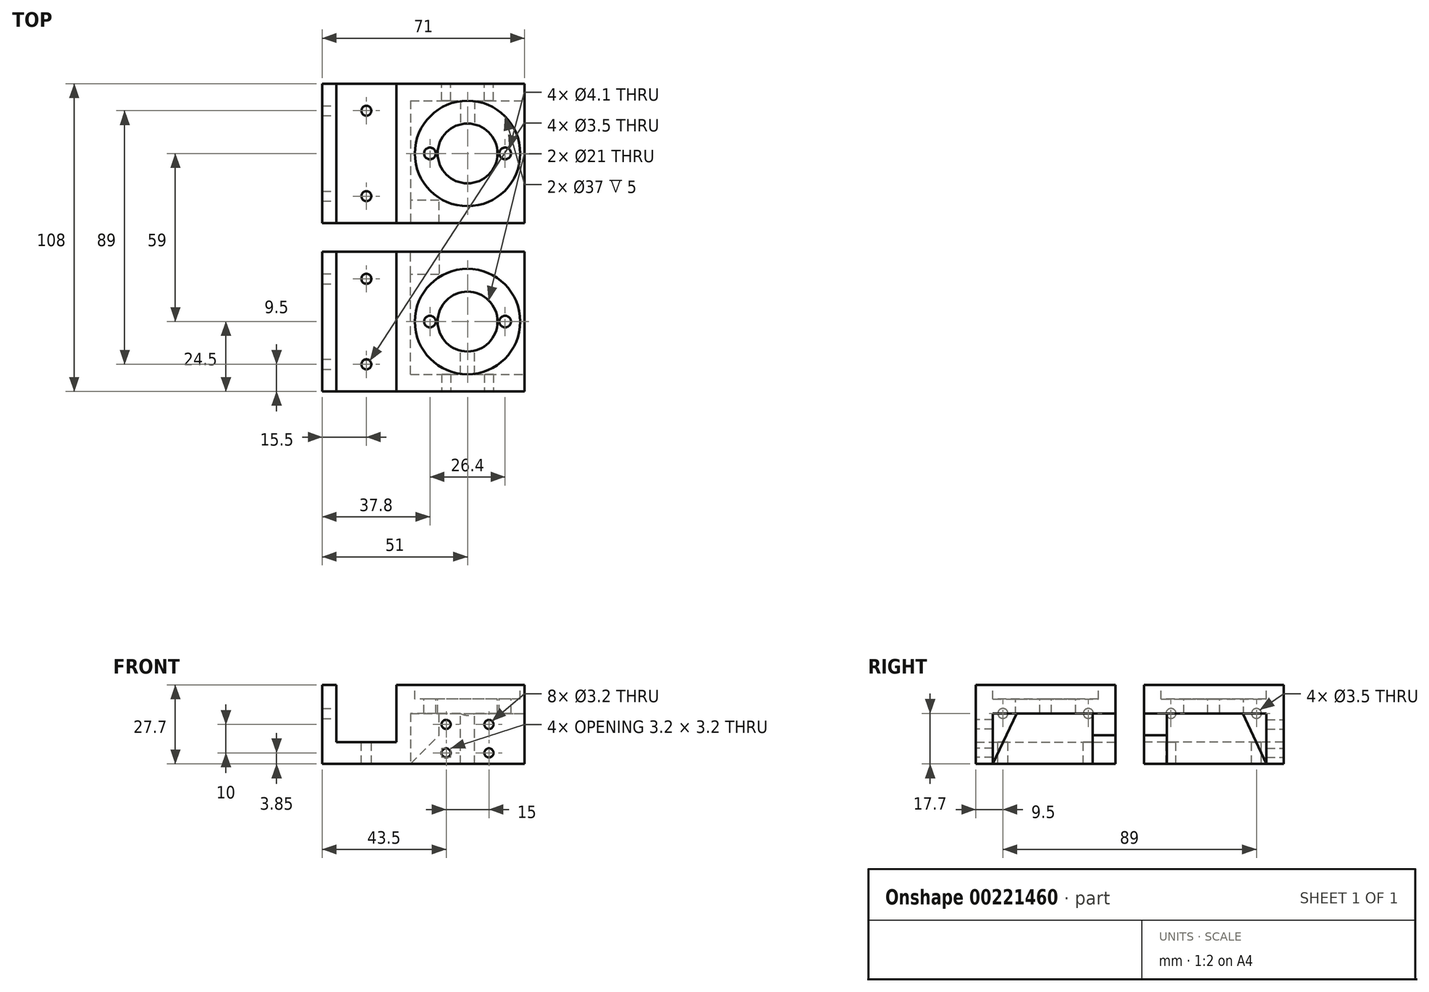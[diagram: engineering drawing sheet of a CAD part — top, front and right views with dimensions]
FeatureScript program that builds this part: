
annotation { "Feature Type Name" : "Feature", "Feature Type Description" : "" }
export const myFeature = defineFeature(function(context is Context, id is Id, definition is map)
    precondition{}
    {
        {
            var Q0;
            Q0=qCreatedBy(makeId("Front.planeOp"),FACE);
            var sketch = newSketch(context, id + "F0", { "sketchPlane" : qUnion([Q0])});
            skLineSegment(sketch, "E0.bottom", {"start": v(0, 0) * mm, "end": v(27, 0) * mm, "construction": true});
            skLineSegment(sketch, "E0.top", {"start": v(0, 27.7) * mm, "end": v(27, 27.7) * mm, "construction": true});
            skLineSegment(sketch, "E0.left", {"start": v(0, 0) * mm, "end": v(0, 27.7) * mm, "construction": true});
            skLineSegment(sketch, "E0.right", {"start": v(27, 0) * mm, "end": v(27, 27.7) * mm, "construction": true});
            skLineSegment(sketch, "E1.bottom", {"start": v(-6.5, 27.7) * mm, "end": v(33.5, 27.7) * mm});
            skLineSegment(sketch, "E1.top", {"start": v(-6.5, 0) * mm, "end": v(33.5, 0) * mm});
            skLineSegment(sketch, "E1.left", {"start": v(-6.5, 27.7) * mm, "end": v(-6.5, 0) * mm});
            skLineSegment(sketch, "E1.right", {"start": v(33.5, 27.7) * mm, "end": v(33.5, 0) * mm});
            skSolve(sketch);
        }
        {
            var Q0;
            Q0=makeQuery(id+"F0.imprint","IMPRINT",FACE,{"disambiguationData":[TD([[makeQuery(id+"F0.imprint","IMPRINT",EDGE,{"derivedFrom":sQuery(id+"F0.wireOp",EDGE,"E0.bottom")}),1.0]])]});
            var Q1;
            Q1=makeQuery(id+"F0.imprint","IMPRINT",FACE,{"disambiguationData":[TD([[makeQuery(id+"F0.imprint","IMPRINT",EDGE,{"derivedFrom":sQuery(id+"F0.wireOp",EDGE,"E1.bottom")}),-1.0]])]});
            extrude(context, id + "F1", {"entities" : qUnion([Q0, Q1]), "depth" : 6 * mm});
        }
        {
            var Q0;
            Q0=makeQuery(id+"F1.opExtrude","CAP_FACE",FACE,{"disambiguationData":[OSD([sQuery(id+"F0.wireOp",EDGE,"E1.bottom"),sQuery(id+"F0.wireOp",EDGE,"E1.top"),sQuery(id+"F0.wireOp",EDGE,"E1.left"),sQuery(id+"F0.wireOp",EDGE,"E1.right")])],"isStart":false});
            var sketch = newSketch(context, id + "F2", { "sketchPlane" : qUnion([Q0])});
            skLineSegment(sketch, "E2.bottom", {"start": v(-6.5, 27.7) * mm, "end": v(33.5, 27.7) * mm});
            skLineSegment(sketch, "E2.top", {"start": v(-6.5, 17.7) * mm, "end": v(33.5, 17.7) * mm});
            skLineSegment(sketch, "E2.left", {"start": v(-6.5, 27.7) * mm, "end": v(-6.5, 17.7) * mm});
            skLineSegment(sketch, "E2.right", {"start": v(33.5, 27.7) * mm, "end": v(33.5, 17.7) * mm});
            skLineSegment(sketch, "E3", {"start": v(13.5, 27.7) * mm, "end": v(13.5, 0) * mm, "construction": true});
            skSolve(sketch);
        }
        {
            var Q0;
            Q0=makeQuery(id+"F2.imprint","IMPRINT",FACE,{"disambiguationData":[TD([[makeQuery(id+"F2.imprint","IMPRINT",EDGE,{"derivedFrom":sQuery(id+"F2.wireOp",EDGE,"E2.bottom")}),-1.0]])]});
            extrude(context, id + "F3", {"entities" : qUnion([Q0]), "operationType" : NewBodyOperationType.ADD, "depth" : 43 * mm});
        }
        {
            var Q0;
            Q0=makeQuery(id+"F3.opExtrude","SWEPT_FACE",FACE,{"disambiguationData":[OSD([sQuery(id+"F2.wireOp",EDGE,"E2.bottom")])]});
            var sketch = newSketch(context, id + "F4", { "sketchPlane" : qUnion([Q0])});
            skCircle(sketch, "E4", {"center": v(13.5, -24.5) * mm, "radius": 18.5 * mm});
            skPoint(sketch, "E4.centerSnap0", {"position": v(13.5, -3) * mm});
            skPoint(sketch, "E4.centerSnap1", {"position": v(-6.5, -24.5) * mm});
            skSolve(sketch);
        }
        {
            var Q0;
            Q0=makeQuery(id+"F4.imprint","IMPRINT",FACE,{"disambiguationData":[TD([[makeQuery(id+"F4.imprint","IMPRINT",EDGE,{"derivedFrom":sQuery(id+"F4.wireOp",EDGE,"E4")}),1.0]])]});
            extrude(context, id + "F5", {"entities" : qUnion([Q0]), "operationType" : NewBodyOperationType.REMOVE, "oppositeDirection" : true, "depth" : 5 * mm});
        }
        {
            var Q0;
            Q0=makeQuery(id+"F5.boolean.opBoolean","COPY",FACE,{"derivedFrom":makeQuery(id+"F5.opExtrude","CAP_FACE",FACE,{"disambiguationData":[OSD([sQuery(id+"F4.wireOp",EDGE,"E4")])],"isStart":false})});
            var sketch = newSketch(context, id + "F6", { "sketchPlane" : qUnion([Q0])});
            skCircle(sketch, "E5", {"center": v(13.5, -24.5) * mm, "radius": 10.5 * mm});
            skLineSegment(sketch, "E6", {"start": v(13.5, -24.5) * mm, "end": v(32, -24.5) * mm, "construction": true});
            skLineSegment(sketch, "E7", {"start": v(13.5, -24.5) * mm, "end": v(-5, -24.5) * mm, "construction": true});
            skCircle(sketch, "E8", {"center": v(13.5, -24.5) * mm, "radius": 13.2 * mm, "construction": true});
            skCircle(sketch, "E9", {"center": v(26.7, -24.5) * mm, "radius": 2.05 * mm});
            skCircle(sketch, "E10", {"center": v(0.3, -24.5) * mm, "radius": 2.05 * mm});
            skSolve(sketch);
        }
        {
            var Q0;
            Q0 = qSketchRegion(id + "F6", true);
            extrude(context, id + "F7", {"entities" : qUnion([Q0]), "operationType" : NewBodyOperationType.REMOVE, "endBound" : BoundingType.THROUGH_ALL, "oppositeDirection" : true, "depth" : 25 * mm});
        }
        {
            var Q0;
            Q0=makeQuery(id+"F3.boolean.opBoolean","MERGE",FACE,{"derivedFrom":[makeQuery(id+"F1.opExtrude","SWEPT_FACE",FACE,{"disambiguationData":[OSD([sQuery(id+"F0.wireOp",EDGE,"E1.left")])]}),makeQuery(id+"F3.opExtrude","SWEPT_FACE",FACE,{"disambiguationData":[OSD([sQuery(id+"F2.wireOp",EDGE,"E2.left")])]})]});
            var sketch = newSketch(context, id + "F8", { "sketchPlane" : qUnion([Q0])});
            skLineSegment(sketch, "E11.bottom", {"start": v(0, 0) * mm, "end": v(49, 0) * mm});
            skLineSegment(sketch, "E11.top", {"start": v(0, 27.7) * mm, "end": v(49, 27.7) * mm});
            skLineSegment(sketch, "E11.left", {"start": v(0, 0) * mm, "end": v(0, 27.7) * mm});
            skLineSegment(sketch, "E11.right", {"start": v(49, 0) * mm, "end": v(49, 27.7) * mm});
            skSolve(sketch);
        }
        {
            var Q0;
            {var subQ1=sQuery(id+"F2.wireOp",EDGE,"E2.top");var subQ2=sQuery(id+"F2.wireOp",EDGE,"E2.left");var subQ3=sQuery(id+"F0.wireOp",EDGE,"E1.left");var subQ8=makeQuery(id+"F3.opExtrude","SWEPT_EDGE",EDGE,{"disambiguationData":[OSD([subQ3,subQ1,subQ2])]});Q0=makeQuery(id+"F8.imprint","IMPRINT",FACE,{"disambiguationData":[TD([[makeQuery(id+"F8.imprint","IMPRINT",EDGE,{"derivedFrom":subQ8}),1.0]])]});}
            var Q1;
            {var subQ12=sQuery(id+"F8.wireOp",EDGE,"E11.left");Q1=makeQuery(id+"F8.imprint","IMPRINT",FACE,{"disambiguationData":[TD([[makeQuery(id+"F8.imprint","IMPRINT",EDGE,{"derivedFrom":subQ12}),1.0]])]});}
            extrude(context, id + "F9", {"entities" : qUnion([Q0, Q1]), "operationType" : NewBodyOperationType.ADD, "depth" : 31 * mm});
        }
        {
            var Q0;
            Q0=makeQuery(id+"F9.boolean.opBoolean","MERGE",FACE,{"derivedFrom":[makeQuery(id+"F3.opExtrude","CAP_FACE",FACE,{"disambiguationData":[OSD([sQuery(id+"F2.wireOp",EDGE,"E2.bottom"),sQuery(id+"F2.wireOp",EDGE,"E2.top"),sQuery(id+"F2.wireOp",EDGE,"E2.left"),sQuery(id+"F2.wireOp",EDGE,"E2.right")])],"isStart":false}),makeQuery(id+"F9.opExtrude","SWEPT_FACE",FACE,{"disambiguationData":[OSD([sQuery(id+"F8.wireOp",EDGE,"E11.right")])]})]});
            var sketch = newSketch(context, id + "F10", { "sketchPlane" : qUnion([Q0])});
            skLineSegment(sketch, "E12", {"start": v(-32.5, 27.7) * mm, "end": v(-32.5, 7.7) * mm});
            skLineSegment(sketch, "E13", {"start": v(-32.5, 7.7) * mm, "end": v(-11.5, 7.7) * mm});
            skLineSegment(sketch, "E14", {"start": v(-11.5, 7.7) * mm, "end": v(-11.5, 27.7) * mm});
            skLineSegment(sketch, "E15", {"start": v(-32.5, 27.7) * mm, "end": v(-11.5, 27.7) * mm});
            skSolve(sketch);
        }
        {
            var Q0;
            Q0=makeQuery(id+"F10.imprint","IMPRINT",FACE,{"disambiguationData":[TD([[makeQuery(id+"F10.imprint","IMPRINT",EDGE,{"derivedFrom":sQuery(id+"F10.wireOp",EDGE,"E12")}),1.0]])]});
            extrude(context, id + "F11", {"entities" : qUnion([Q0]), "operationType" : NewBodyOperationType.REMOVE, "endBound" : BoundingType.THROUGH_ALL, "oppositeDirection" : true, "depth" : 25 * mm});
        }
        {
            var Q0;
            Q0=makeQuery(id+"F3.opExtrude","SWEPT_FACE",FACE,{"disambiguationData":[OSD([sQuery(id+"F2.wireOp",EDGE,"E2.top")])]});
            var sketch = newSketch(context, id + "F12", { "sketchPlane" : qUnion([Q0])});
            skLineSegment(sketch, "E16.bottom", {"start": v(11, 6) * mm, "end": v(16, 6) * mm});
            skLineSegment(sketch, "E16.left", {"start": v(11, 6) * mm, "end": v(11, 14.3) * mm});
            skLineSegment(sketch, "E16.right", {"start": v(16, 6) * mm, "end": v(16, 14.3) * mm});
            skArc(sketch, "E17", {"start": v(16, 14.3) * mm, "mid": v(13.5, 14) * mm, "end": v(11, 14.3) * mm});
            skPoint(sketch, "E18", {"position": v(13.5, 6) * mm});
            skSolve(sketch);
        }
        {
            var Q0;
            Q0=makeQuery(id+"F12.imprint","IMPRINT",FACE,{"disambiguationData":[TD([[makeQuery(id+"F12.imprint","IMPRINT",EDGE,{"derivedFrom":sQuery(id+"F12.wireOp",EDGE,"E16.bottom")}),1.0]])]});
            var Q1;
            Q1=makeQuery(id+"F9.boolean.opBoolean","MERGE",FACE,{"derivedFrom":[makeQuery(id+"F1.opExtrude","SWEPT_FACE",FACE,{"disambiguationData":[OSD([sQuery(id+"F0.wireOp",EDGE,"E1.top")])]}),makeQuery(id+"F9.opExtrude","SWEPT_FACE",FACE,{"disambiguationData":[OSD([sQuery(id+"F8.wireOp",EDGE,"E11.bottom")])]})]});
            extrude(context, id + "F13", {"entities" : qUnion([Q0]), "operationType" : NewBodyOperationType.ADD, "endBound" : BoundingType.UP_TO_SURFACE, "endBoundEntityFace" : qUnion([Q1]), "depth" : 25 * mm});
        }
        {
            var Q0;
            Q0=makeQuery(id+"F13.opExtrude","SWEPT_FACE",FACE,{"disambiguationData":[OSD([sQuery(id+"F12.wireOp",EDGE,"E16.right")])]});
            var sketch = newSketch(context, id + "F14", { "sketchPlane" : qUnion([Q0])});
            skLineSegment(sketch, "E19", {"start": v(-14.3, 17.7) * mm, "end": v(-6, 0) * mm});
            skLineSegment(sketch, "E20", {"start": v(-6, 0) * mm, "end": v(-6, 17.7) * mm});
            skLineSegment(sketch, "E21", {"start": v(-6, 17.7) * mm, "end": v(-14.3, 17.7) * mm});
            skSolve(sketch);
        }
        {
            var Q0;
            Q0=makeQuery(id+"F14.imprint","IMPRINT",FACE,{"disambiguationData":[TD([[makeQuery(id+"F14.imprint","IMPRINT",EDGE,{"derivedFrom":sQuery(id+"F14.wireOp",EDGE,"E19")}),-1.0]])]});
            var Q1;
            Q1=makeQuery(id+"F13.opExtrude","SWEPT_FACE",FACE,{"disambiguationData":[OSD([sQuery(id+"F12.wireOp",EDGE,"E16.left")])]});
            extrude(context, id + "F15", {"entities" : qUnion([Q0]), "operationType" : NewBodyOperationType.REMOVE, "endBound" : BoundingType.UP_TO_SURFACE, "oppositeDirection" : true, "endBoundEntityFace" : qUnion([Q1]), "depth" : 25 * mm});
        }
        {
            var Q0;
            Q0=makeQuery(id+"F9.opExtrude","CAP_FACE",FACE,{"disambiguationData":[OSD([sQuery(id+"F8.wireOp",EDGE,"E11.bottom"),sQuery(id+"F8.wireOp",EDGE,"E11.top"),sQuery(id+"F8.wireOp",EDGE,"E11.left"),sQuery(id+"F8.wireOp",EDGE,"E11.right")])],"isStart":true});
            var sketch = newSketch(context, id + "F16", { "sketchPlane" : qUnion([Q0])});
            skLineSegment(sketch, "E22.bottom", {"start": v(-49, 17.7) * mm, "end": v(-41, 17.7) * mm});
            skLineSegment(sketch, "E22.top", {"start": v(-49, 0) * mm, "end": v(-41, 0) * mm});
            skLineSegment(sketch, "E22.left", {"start": v(-49, 17.7) * mm, "end": v(-49, 0) * mm});
            skLineSegment(sketch, "E22.right", {"start": v(-41, 17.7) * mm, "end": v(-41, 0) * mm});
            skSolve(sketch);
        }
        {
            var Q0;
            Q0=makeQuery(id+"F16.imprint","IMPRINT",FACE,{"disambiguationData":[TD([[makeQuery(id+"F16.imprint","IMPRINT",EDGE,{"derivedFrom":sQuery(id+"F16.wireOp",EDGE,"E22.bottom")}),-1.0]])]});
            var Q1;
            Q1=makeQuery(id+"F16.imprint","IMPRINT",FACE,{"disambiguationData":[TD([[makeQuery(id+"F16.imprint","IMPRINT",EDGE,{"derivedFrom":sQuery(id+"F16.wireOp",EDGE,"8BEWw2aY-geet-BJQ8-Mbal-S3a0Wca1nJoR.bottom")}),-1.0]])]});
            extrude(context, id + "F17", {"entities" : qUnion([Q0, Q1]), "operationType" : NewBodyOperationType.ADD, "depth" : 10 * mm});
        }
        {
            var Q0;
            Q0=makeQuery(id+"F11.boolean.opBoolean","COPY",FACE,{"derivedFrom":makeQuery(id+"F11.opExtrude","SWEPT_FACE",FACE,{"disambiguationData":[OSD([sQuery(id+"F10.wireOp",EDGE,"E13")])]})});
            var sketch = newSketch(context, id + "F18", { "sketchPlane" : qUnion([Q0])});
            skLineSegment(sketch, "E23", {"start": v(-22, 0) * mm, "end": v(-22, -49) * mm, "construction": true});
            skCircle(sketch, "E24", {"center": v(-22, -9.5) * mm, "radius": 1.75 * mm});
            skCircle(sketch, "E25", {"center": v(-22, -39.5) * mm, "radius": 1.75 * mm});
            skSolve(sketch);
        }
        {
            var Q0;
            Q0=makeQuery(id+"F18.imprint","IMPRINT",FACE,{"disambiguationData":[TD([[makeQuery(id+"F18.imprint","IMPRINT",EDGE,{"derivedFrom":sQuery(id+"F18.wireOp",EDGE,"E25")}),1.0]])]});
            var Q1;
            Q1=makeQuery(id+"F18.imprint","IMPRINT",FACE,{"disambiguationData":[TD([[makeQuery(id+"F18.imprint","IMPRINT",EDGE,{"derivedFrom":sQuery(id+"F18.wireOp",EDGE,"E24")}),1.0]])]});
            extrude(context, id + "F19", {"entities" : qUnion([Q0, Q1]), "operationType" : NewBodyOperationType.REMOVE, "endBound" : BoundingType.THROUGH_ALL, "oppositeDirection" : true, "depth" : 25 * mm});
        }
        {
            var Q0;
            Q0=makeQuery(id+"F11.boolean.opBoolean","COPY",FACE,{"derivedFrom":makeQuery(id+"F11.opExtrude","SWEPT_FACE",FACE,{"disambiguationData":[OSD([sQuery(id+"F10.wireOp",EDGE,"E12")])]})});
            var sketch = newSketch(context, id + "F20", { "sketchPlane" : qUnion([Q0])});
            skLineSegment(sketch, "E26", {"start": v(-49, 17.7) * mm, "end": v(0, 17.7) * mm, "construction": true});
            skCircle(sketch, "E27", {"center": v(-39.5, 17.7) * mm, "radius": 1.75 * mm});
            skCircle(sketch, "E28", {"center": v(-9.5, 17.7) * mm, "radius": 1.75 * mm});
            skSolve(sketch);
        }
        {
            var Q0;
            Q0=makeQuery(id+"F20.imprint","IMPRINT",FACE,{"disambiguationData":[TD([[makeQuery(id+"F20.imprint","IMPRINT",EDGE,{"derivedFrom":sQuery(id+"F20.wireOp",EDGE,"E27")}),1.0]])]});
            var Q1;
            Q1=makeQuery(id+"F20.imprint","IMPRINT",FACE,{"disambiguationData":[TD([[makeQuery(id+"F20.imprint","IMPRINT",EDGE,{"derivedFrom":sQuery(id+"F20.wireOp",EDGE,"E28")}),1.0]])]});
            extrude(context, id + "F21", {"entities" : qUnion([Q0, Q1]), "operationType" : NewBodyOperationType.REMOVE, "endBound" : BoundingType.THROUGH_ALL, "oppositeDirection" : true, "depth" : 25 * mm});
        }
        {
            var Q0;
            {var subQ2=sQuery(id+"F0.wireOp",EDGE,"E1.top");var subQ3=makeQuery(id+"F1.opExtrude","SWEPT_FACE",FACE,{"disambiguationData":[OSD([subQ2])]});var subQ4=sQuery(id+"F0.wireOp",EDGE,"E1.right");var subQ5=sQuery(id+"F0.wireOp",EDGE,"E1.left");Q0=makeQuery(id+"F13.boolean.opBoolean","SPLIT",FACE,{"disambiguationData":[TD([makeQuery(id+"F13.opExtrude","SWEPT_FACE",FACE,{"disambiguationData":[OSD([sQuery(id+"F12.wireOp",EDGE,"E16.left")])]})])],"derivedFrom":makeQuery(id+"F3.boolean.opBoolean","SPLIT",FACE,{"disambiguationData":[TD([subQ3])],"derivedFrom":makeQuery(id+"F1.opExtrude","CAP_FACE",FACE,{"disambiguationData":[OSD([sQuery(id+"F0.wireOp",EDGE,"E1.bottom"),subQ2,subQ5,subQ4])],"isStart":false})})});}
            var sketch = newSketch(context, id + "F22", { "sketchPlane" : qUnion([Q0])});
            skLineSegment(sketch, "E29.bottom", {"start": v(6, 13.85) * mm, "end": v(21, 13.85) * mm, "construction": true});
            skLineSegment(sketch, "E29.top", {"start": v(6, 3.85) * mm, "end": v(21, 3.85) * mm, "construction": true});
            skLineSegment(sketch, "E29.left", {"start": v(6, 13.85) * mm, "end": v(6, 3.85) * mm, "construction": true});
            skLineSegment(sketch, "E29.right", {"start": v(21, 13.85) * mm, "end": v(21, 3.85) * mm, "construction": true});
            skPoint(sketch, "E30", {"position": v(6, 8.85) * mm});
            skPoint(sketch, "E31", {"position": v(13.5, 13.85) * mm});
            skPoint(sketch, "E32", {"position": v(11, 8.85) * mm});
            skSolve(sketch);
        }
        {
            var Q0;
            Q0=sQuery(id+"F22.wireOp",VERTEX,"E29.left.end");
            var Q1;
            Q1=sQuery(id+"F22.wireOp",VERTEX,"E29.left.start");
            var Q2;
            Q2=sQuery(id+"F22.wireOp",VERTEX,"E29.right.start");
            var Q3;
            Q3=sQuery(id+"F22.wireOp",VERTEX,"E29.right.end");
            var Q4;
            Q4=makeQuery(id+"F1.opExtrude","SWEPT_BODY",BODY,{"disambiguationData":[OSD([sQuery(id+"F0.wireOp",EDGE,"E1.bottom"),sQuery(id+"F0.wireOp",EDGE,"E1.top"),sQuery(id+"F0.wireOp",EDGE,"E1.left"),sQuery(id+"F0.wireOp",EDGE,"E1.right")])]});
            hole(context, id + "F23", {"style" : HoleStyle.SIMPLE, "endStyle" : HoleEndStyle.THROUGH, "holeDiameter" : 3.2 * mm, "locations" : qUnion([Q0, Q1, Q2, Q3]), "scope" : qUnion([Q4]), "isTappedThrough" : true});
        }
        {
            var Q0;
            Q0=makeQuery(id+"F17.opExtrude","CAP_EDGE",EDGE,{"disambiguationData":[OSD([sQuery(id+"F16.wireOp",EDGE,"E22.top")])],"isStart":false});
            chamfer(context, id + "F24", {"entities" : qUnion([Q0]), "width" : 10 * mm, "tangentPropagation" : true});
        }
        {
            var Q0;
            Q0=makeQuery(id+"F17.boolean.opBoolean","MERGE",FACE,{"derivedFrom":[makeQuery(id+"F9.boolean.opBoolean","MERGE",FACE,{"derivedFrom":[makeQuery(id+"F3.opExtrude","CAP_FACE",FACE,{"disambiguationData":[OSD([sQuery(id+"F2.wireOp",EDGE,"E2.bottom"),sQuery(id+"F2.wireOp",EDGE,"E2.top"),sQuery(id+"F2.wireOp",EDGE,"E2.left"),sQuery(id+"F2.wireOp",EDGE,"E2.right")])],"isStart":false}),makeQuery(id+"F9.opExtrude","SWEPT_FACE",FACE,{"disambiguationData":[OSD([sQuery(id+"F8.wireOp",EDGE,"E11.right")])]})]}),makeQuery(id+"F17.opExtrude","SWEPT_FACE",FACE,{"disambiguationData":[OSD([sQuery(id+"F16.wireOp",EDGE,"E22.left")])]})]});
            cPlane(context, id + "F25", {"entities" : qUnion([Q0]), "cplaneType" : CPlaneType.OFFSET, "offset" : 5 * mm, "width" : 150 * mm, "height" : 150 * mm});
        }
        {
            var Q0;
            Q0=makeQuery(id+"F1.opExtrude","SWEPT_BODY",BODY,{"disambiguationData":[OSD([sQuery(id+"F0.wireOp",EDGE,"E1.bottom"),sQuery(id+"F0.wireOp",EDGE,"E1.top"),sQuery(id+"F0.wireOp",EDGE,"E1.left"),sQuery(id+"F0.wireOp",EDGE,"E1.right")])]});
            var Q1;
            Q1=qCreatedBy(id+"F25.planeOp",FACE);
            mirror(context, id + "F26", {"entities" : qUnion([Q0]), "mirrorPlane" : qUnion([Q1])});
        }
    });
